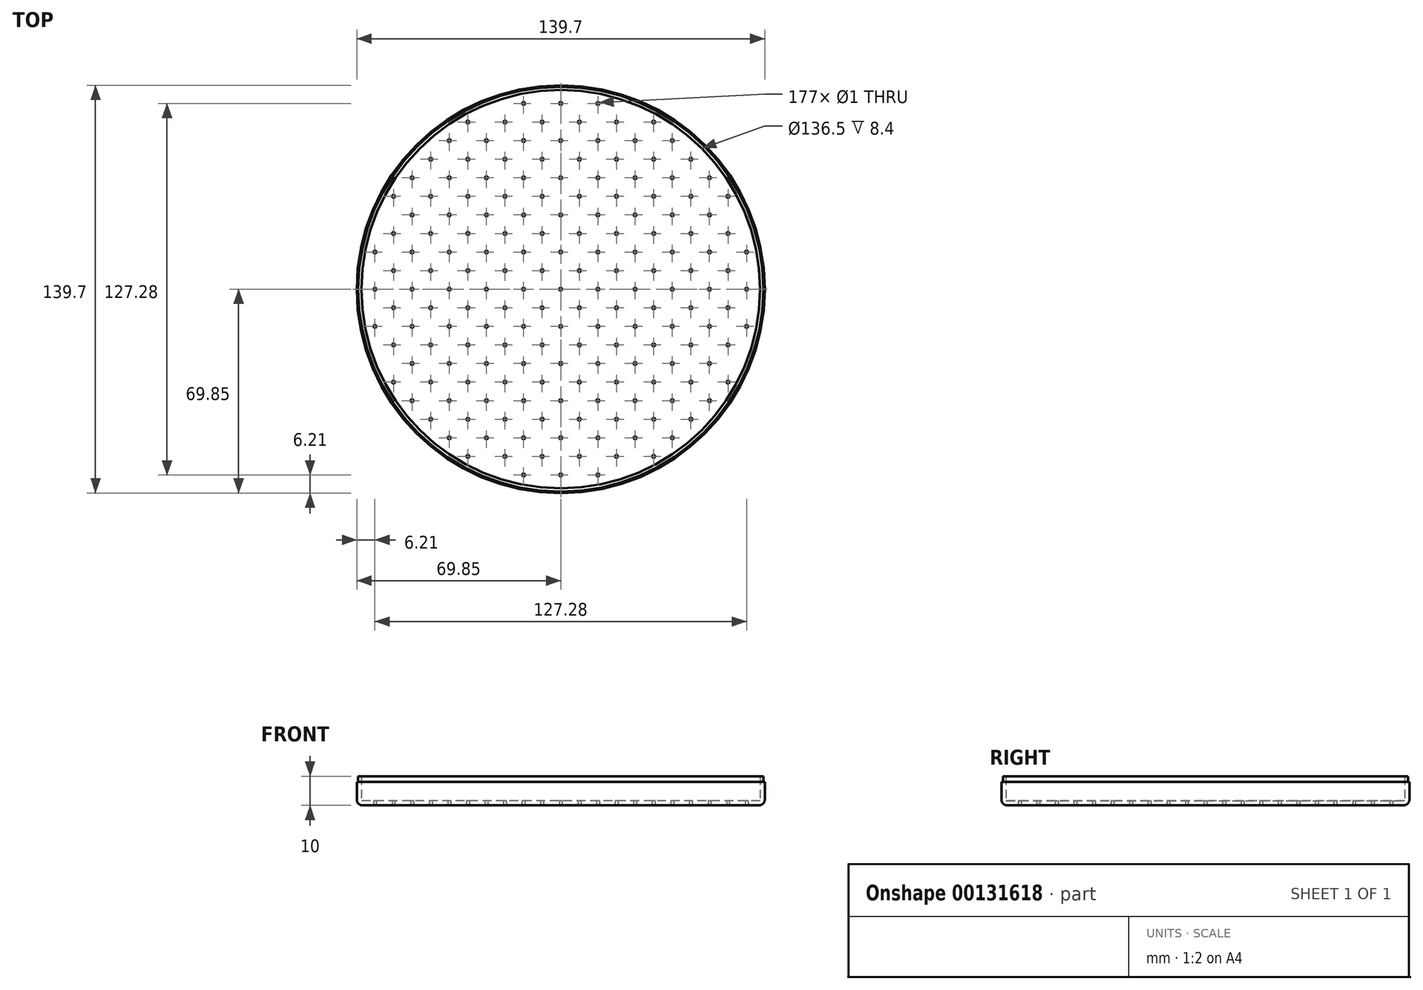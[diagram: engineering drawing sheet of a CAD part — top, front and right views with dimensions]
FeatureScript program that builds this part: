
annotation { "Feature Type Name" : "Feature", "Feature Type Description" : "" }
export const myFeature = defineFeature(function(context is Context, id is Id, definition is map)
    precondition{}
    {
        {
            var Q0;
            Q0=qCreatedBy(makeId("Top.planeOp"),FACE);
            var sketch = newSketch(context, id + "F0", { "sketchPlane" : qUnion([Q0])});
            skCircle(sketch, "E0", {"center": v(0, 0) * mm, "radius": 69.85 * mm});
            skSolve(sketch);
        }
        {
            var Q0;
            Q0=qSketchRegion(id+"F0",true);
            extrude(context, id + "F1", {"entities" : qUnion([Q0]), "depth" : 10 * mm});
        }
        {
            var Q0;
            Q0=makeQuery(id+"F1.opExtrude","CAP_FACE",FACE,{"disambiguationData":[OSD([sQuery(id+"F0.wireOp",EDGE,"E0")])],"isStart":false});
            shell(context, id + "F2", {"entities" : qUnion([Q0]), "thickness" : 1.6 * mm});
        }
        {
            var Q0;
            Q0=makeQuery(id+"F1.opExtrude","CAP_FACE",FACE,{"disambiguationData":[OSD([sQuery(id+"F0.wireOp",EDGE,"E0")])],"isStart":true});
            var sketch = newSketch(context, id + "F3", { "sketchPlane" : qUnion([Q0])});
            skCircle(sketch, "E1", {"center": v(-6.36, 6.36) * mm, "radius": 0.5 * mm});
            skCircle(sketch, "E2.1.0.0", {"center": v(-19.1, 6.36) * mm, "radius": 0.5 * mm});
            skCircle(sketch, "E2.2.0.0", {"center": v(-31.82, 6.36) * mm, "radius": 0.5 * mm});
            skCircle(sketch, "E2.3.0.0", {"center": v(-44.55, 6.36) * mm, "radius": 0.5 * mm});
            skCircle(sketch, "E2.4.0.0", {"center": v(-57.28, 6.36) * mm, "radius": 0.5 * mm});
            skLineSegment(sketch, "E2.direction1", {"start": v(-6.36, 6.36) * mm, "end": v(-19.1, 6.36) * mm, "construction": true});
            skCircle(sketch, "E3", {"center": v(0, 0) * mm, "radius": 0.5 * mm});
            skCircle(sketch, "E4.1.0.0", {"center": v(-12.73, 0) * mm, "radius": 0.5 * mm});
            skCircle(sketch, "E4.2.0.0", {"center": v(-25.46, 0) * mm, "radius": 0.5 * mm});
            skCircle(sketch, "E4.3.0.0", {"center": v(-38.18, 0) * mm, "radius": 0.5 * mm});
            skCircle(sketch, "E4.4.0.0", {"center": v(-50.91, 0) * mm, "radius": 0.5 * mm});
            skCircle(sketch, "E4.5.0.0", {"center": v(-63.64, 0) * mm, "radius": 0.5 * mm});
            skLineSegment(sketch, "E4.direction1", {"start": v(0, 0) * mm, "end": v(-12.73, 0) * mm, "construction": true});
            skLineSegment(sketch, "E5.0.1.0", {"start": v(0, 12.73) * mm, "end": v(-12.73, 12.73) * mm, "construction": true});
            skLineSegment(sketch, "E5.0.1.1", {"start": v(-6.36, 19.1) * mm, "end": v(-19.1, 19.1) * mm, "construction": true});
            skCircle(sketch, "E5.0.1.2", {"center": v(-50.91, 12.73) * mm, "radius": 0.5 * mm});
            skCircle(sketch, "E5.0.1.3", {"center": v(-31.82, 19.1) * mm, "radius": 0.5 * mm});
            skCircle(sketch, "E5.0.1.4", {"center": v(-44.55, 19.1) * mm, "radius": 0.5 * mm});
            skCircle(sketch, "E5.0.1.5", {"center": v(-38.18, 12.73) * mm, "radius": 0.5 * mm});
            skCircle(sketch, "E5.0.1.6", {"center": v(-57.28, 19.1) * mm, "radius": 0.5 * mm});
            skCircle(sketch, "E5.0.1.7", {"center": v(-25.46, 12.73) * mm, "radius": 0.5 * mm});
            skCircle(sketch, "E5.0.1.8", {"center": v(-63.64, 12.73) * mm, "radius": 0.5 * mm});
            skCircle(sketch, "E5.0.1.9", {"center": v(-19.1, 19.1) * mm, "radius": 0.5 * mm});
            skCircle(sketch, "E5.0.1.10", {"center": v(-6.36, 19.1) * mm, "radius": 0.5 * mm});
            skCircle(sketch, "E5.0.1.11", {"center": v(0, 12.73) * mm, "radius": 0.5 * mm});
            skCircle(sketch, "E5.0.1.12", {"center": v(-12.73, 12.73) * mm, "radius": 0.5 * mm});
            skLineSegment(sketch, "E5.0.2.0", {"start": v(0, 25.46) * mm, "end": v(-12.73, 25.46) * mm, "construction": true});
            skLineSegment(sketch, "E5.0.2.1", {"start": v(-6.36, 31.82) * mm, "end": v(-19.1, 31.82) * mm, "construction": true});
            skCircle(sketch, "E5.0.2.2", {"center": v(-50.91, 25.46) * mm, "radius": 0.5 * mm});
            skCircle(sketch, "E5.0.2.3", {"center": v(-31.82, 31.82) * mm, "radius": 0.5 * mm});
            skCircle(sketch, "E5.0.2.4", {"center": v(-44.55, 31.82) * mm, "radius": 0.5 * mm});
            skCircle(sketch, "E5.0.2.5", {"center": v(-38.18, 25.46) * mm, "radius": 0.5 * mm});
            skCircle(sketch, "E5.0.2.6", {"center": v(-57.28, 31.82) * mm, "radius": 0.5 * mm});
            skCircle(sketch, "E5.0.2.7", {"center": v(-25.46, 25.46) * mm, "radius": 0.5 * mm});
            skCircle(sketch, "E5.0.2.9", {"center": v(-19.1, 31.82) * mm, "radius": 0.5 * mm});
            skCircle(sketch, "E5.0.2.10", {"center": v(-6.36, 31.82) * mm, "radius": 0.5 * mm});
            skCircle(sketch, "E5.0.2.11", {"center": v(0, 25.46) * mm, "radius": 0.5 * mm});
            skCircle(sketch, "E5.0.2.12", {"center": v(-12.73, 25.46) * mm, "radius": 0.5 * mm});
            skLineSegment(sketch, "E5.0.3.0", {"start": v(0, 38.18) * mm, "end": v(-12.73, 38.18) * mm, "construction": true});
            skLineSegment(sketch, "E5.0.3.1", {"start": v(-6.36, 44.55) * mm, "end": v(-19.1, 44.55) * mm, "construction": true});
            skCircle(sketch, "E5.0.3.2", {"center": v(-50.91, 38.18) * mm, "radius": 0.5 * mm});
            skCircle(sketch, "E5.0.3.3", {"center": v(-31.82, 44.55) * mm, "radius": 0.5 * mm});
            skCircle(sketch, "E5.0.3.4", {"center": v(-44.55, 44.55) * mm, "radius": 0.5 * mm});
            skCircle(sketch, "E5.0.3.5", {"center": v(-38.18, 38.18) * mm, "radius": 0.5 * mm});
            skCircle(sketch, "E5.0.3.7", {"center": v(-25.46, 38.18) * mm, "radius": 0.5 * mm});
            skCircle(sketch, "E5.0.3.9", {"center": v(-19.1, 44.55) * mm, "radius": 0.5 * mm});
            skCircle(sketch, "E5.0.3.10", {"center": v(-6.36, 44.55) * mm, "radius": 0.5 * mm});
            skCircle(sketch, "E5.0.3.11", {"center": v(0, 38.18) * mm, "radius": 0.5 * mm});
            skCircle(sketch, "E5.0.3.12", {"center": v(-12.73, 38.18) * mm, "radius": 0.5 * mm});
            skLineSegment(sketch, "E5.0.4.0", {"start": v(0, 50.91) * mm, "end": v(-12.73, 50.91) * mm, "construction": true});
            skLineSegment(sketch, "E5.0.4.1", {"start": v(-6.36, 57.28) * mm, "end": v(-19.1, 57.28) * mm, "construction": true});
            skCircle(sketch, "E5.0.4.3", {"center": v(-31.82, 57.28) * mm, "radius": 0.5 * mm});
            skCircle(sketch, "E5.0.4.5", {"center": v(-38.18, 50.91) * mm, "radius": 0.5 * mm});
            skCircle(sketch, "E5.0.4.7", {"center": v(-25.46, 50.91) * mm, "radius": 0.5 * mm});
            skCircle(sketch, "E5.0.4.9", {"center": v(-19.1, 57.28) * mm, "radius": 0.5 * mm});
            skCircle(sketch, "E5.0.4.10", {"center": v(-6.36, 57.28) * mm, "radius": 0.5 * mm});
            skCircle(sketch, "E5.0.4.11", {"center": v(0, 50.91) * mm, "radius": 0.5 * mm});
            skCircle(sketch, "E5.0.4.12", {"center": v(-12.73, 50.91) * mm, "radius": 0.5 * mm});
            skLineSegment(sketch, "E5.0.5.0", {"start": v(0, 63.64) * mm, "end": v(-12.73, 63.64) * mm, "construction": true});
            skCircle(sketch, "E5.0.5.11", {"center": v(0, 63.64) * mm, "radius": 0.5 * mm});
            skCircle(sketch, "E5.0.5.12", {"center": v(-12.73, 63.64) * mm, "radius": 0.5 * mm});
            skLineSegment(sketch, "E5.direction1", {"start": v(-63.64, 0) * mm, "end": v(-38.64, 0) * mm, "construction": true});
            skLineSegment(sketch, "E5.direction2", {"start": v(-63.64, 0) * mm, "end": v(-63.64, 12.73) * mm, "construction": true});
            skCircle(sketch, "E6.MirrorC", {"center": v(63.64, 0) * mm, "radius": 0.5 * mm});
            skCircle(sketch, "E7.MirrorC", {"center": v(6.36, 31.82) * mm, "radius": 0.5 * mm});
            skCircle(sketch, "E8.MirrorC", {"center": v(12.73, 0) * mm, "radius": 0.5 * mm});
            skCircle(sketch, "E9.MirrorC", {"center": v(19.1, 6.36) * mm, "radius": 0.5 * mm});
            skCircle(sketch, "E10.MirrorC", {"center": v(6.36, 6.36) * mm, "radius": 0.5 * mm});
            skCircle(sketch, "E11.MirrorC", {"center": v(19.1, 31.82) * mm, "radius": 0.5 * mm});
            skCircle(sketch, "E12.MirrorC", {"center": v(19.1, 19.1) * mm, "radius": 0.5 * mm});
            skCircle(sketch, "E13.MirrorC", {"center": v(12.73, 50.91) * mm, "radius": 0.5 * mm});
            skCircle(sketch, "E14.MirrorC", {"center": v(12.73, 12.73) * mm, "radius": 0.5 * mm});
            skCircle(sketch, "E15.MirrorC", {"center": v(12.73, 38.18) * mm, "radius": 0.5 * mm});
            skCircle(sketch, "E16.MirrorC", {"center": v(19.1, 57.28) * mm, "radius": 0.5 * mm});
            skCircle(sketch, "E17.MirrorC", {"center": v(12.73, 25.46) * mm, "radius": 0.5 * mm});
            skCircle(sketch, "E18.MirrorC", {"center": v(6.36, 44.55) * mm, "radius": 0.5 * mm});
            skCircle(sketch, "E19.MirrorC", {"center": v(12.73, 63.64) * mm, "radius": 0.5 * mm});
            skCircle(sketch, "E20.MirrorC", {"center": v(63.64, 12.73) * mm, "radius": 0.5 * mm});
            skCircle(sketch, "E21.MirrorC", {"center": v(6.36, 19.1) * mm, "radius": 0.5 * mm});
            skCircle(sketch, "E22.MirrorC", {"center": v(19.1, 44.55) * mm, "radius": 0.5 * mm});
            skCircle(sketch, "E23.MirrorC", {"center": v(6.36, 57.28) * mm, "radius": 0.5 * mm});
            skCircle(sketch, "E24.MirrorC", {"center": v(31.82, 57.28) * mm, "radius": 0.5 * mm});
            skCircle(sketch, "E25.MirrorC", {"center": v(57.28, 19.1) * mm, "radius": 0.5 * mm});
            skCircle(sketch, "E26.MirrorC", {"center": v(44.55, 44.55) * mm, "radius": 0.5 * mm});
            skLineSegment(sketch, "E27.MirrorCS", {"start": v(0, 0) * mm, "end": v(12.73, 0) * mm, "construction": true});
            skCircle(sketch, "E28.MirrorC", {"center": v(50.91, 0) * mm, "radius": 0.5 * mm});
            skCircle(sketch, "E29.MirrorC", {"center": v(38.18, 0) * mm, "radius": 0.5 * mm});
            skCircle(sketch, "E30.MirrorC", {"center": v(25.46, 0) * mm, "radius": 0.5 * mm});
            skCircle(sketch, "E31.MirrorC", {"center": v(57.28, 6.36) * mm, "radius": 0.5 * mm});
            skCircle(sketch, "E32.MirrorC", {"center": v(44.55, 6.36) * mm, "radius": 0.5 * mm});
            skCircle(sketch, "E33.MirrorC", {"center": v(31.82, 6.36) * mm, "radius": 0.5 * mm});
            skCircle(sketch, "E34.MirrorC", {"center": v(50.91, 12.73) * mm, "radius": 0.5 * mm});
            skCircle(sketch, "E35.MirrorC", {"center": v(38.18, 12.73) * mm, "radius": 0.5 * mm});
            skCircle(sketch, "E36.MirrorC", {"center": v(31.82, 44.55) * mm, "radius": 0.5 * mm});
            skCircle(sketch, "E37.MirrorC", {"center": v(25.46, 25.46) * mm, "radius": 0.5 * mm});
            skCircle(sketch, "E38.MirrorC", {"center": v(44.55, 19.1) * mm, "radius": 0.5 * mm});
            skCircle(sketch, "E39.MirrorC", {"center": v(50.91, 38.18) * mm, "radius": 0.5 * mm});
            skCircle(sketch, "E40.MirrorC", {"center": v(25.46, 38.18) * mm, "radius": 0.5 * mm});
            skCircle(sketch, "E41.MirrorC", {"center": v(31.82, 19.1) * mm, "radius": 0.5 * mm});
            skCircle(sketch, "E42.MirrorC", {"center": v(38.18, 25.46) * mm, "radius": 0.5 * mm});
            skCircle(sketch, "E43.MirrorC", {"center": v(38.18, 50.91) * mm, "radius": 0.5 * mm});
            skCircle(sketch, "E44.MirrorC", {"center": v(38.18, 38.18) * mm, "radius": 0.5 * mm});
            skCircle(sketch, "E45.MirrorC", {"center": v(31.82, 31.82) * mm, "radius": 0.5 * mm});
            skCircle(sketch, "E46.MirrorC", {"center": v(50.91, 25.46) * mm, "radius": 0.5 * mm});
            skCircle(sketch, "E47.MirrorC", {"center": v(25.46, 12.73) * mm, "radius": 0.5 * mm});
            skCircle(sketch, "E48.MirrorC", {"center": v(25.46, 50.91) * mm, "radius": 0.5 * mm});
            skCircle(sketch, "E49.MirrorC", {"center": v(44.55, 31.82) * mm, "radius": 0.5 * mm});
            skCircle(sketch, "E50.MirrorC", {"center": v(57.28, 31.82) * mm, "radius": 0.5 * mm});
            skLineSegment(sketch, "E51.MirrorCS", {"start": v(0, 25.46) * mm, "end": v(12.73, 25.46) * mm, "construction": true});
            skLineSegment(sketch, "E52.MirrorCS", {"start": v(0, 63.64) * mm, "end": v(12.73, 63.64) * mm, "construction": true});
            skLineSegment(sketch, "E53.MirrorCS", {"start": v(6.36, 6.36) * mm, "end": v(19.1, 6.36) * mm, "construction": true});
            skLineSegment(sketch, "E54.MirrorCS", {"start": v(6.36, 57.28) * mm, "end": v(19.1, 57.28) * mm, "construction": true});
            skLineSegment(sketch, "E55.MirrorCS", {"start": v(6.36, 19.1) * mm, "end": v(19.1, 19.1) * mm, "construction": true});
            skLineSegment(sketch, "E56.MirrorCS", {"start": v(0, 50.91) * mm, "end": v(12.73, 50.91) * mm, "construction": true});
            skLineSegment(sketch, "E57.MirrorCS", {"start": v(0, 12.73) * mm, "end": v(12.73, 12.73) * mm, "construction": true});
            skLineSegment(sketch, "E58.MirrorCS", {"start": v(0, 38.18) * mm, "end": v(12.73, 38.18) * mm, "construction": true});
            skLineSegment(sketch, "E59.MirrorCS", {"start": v(63.64, 0) * mm, "end": v(38.64, 0) * mm, "construction": true});
            skLineSegment(sketch, "E60.MirrorCS", {"start": v(6.36, 44.55) * mm, "end": v(19.1, 44.55) * mm, "construction": true});
            skLineSegment(sketch, "E61.MirrorCS", {"start": v(63.64, 0) * mm, "end": v(63.64, 12.73) * mm, "construction": true});
            skLineSegment(sketch, "E62.MirrorCS", {"start": v(6.36, 31.82) * mm, "end": v(19.1, 31.82) * mm, "construction": true});
            skCircle(sketch, "E63.MirrorC", {"center": v(0, -63.64) * mm, "radius": 0.5 * mm});
            skCircle(sketch, "E64.MirrorC", {"center": v(0, -25.46) * mm, "radius": 0.5 * mm});
            skCircle(sketch, "E65.MirrorC", {"center": v(0, -38.18) * mm, "radius": 0.5 * mm});
            skCircle(sketch, "E66.MirrorC", {"center": v(0, -50.91) * mm, "radius": 0.5 * mm});
            skCircle(sketch, "E67.MirrorC", {"center": v(0, -12.73) * mm, "radius": 0.5 * mm});
            skCircle(sketch, "E68.MirrorC", {"center": v(-6.36, -31.82) * mm, "radius": 0.5 * mm});
            skCircle(sketch, "E69.MirrorC", {"center": v(6.36, -19.1) * mm, "radius": 0.5 * mm});
            skCircle(sketch, "E70.MirrorC", {"center": v(6.36, -6.36) * mm, "radius": 0.5 * mm});
            skCircle(sketch, "E71.MirrorC", {"center": v(12.73, -38.18) * mm, "radius": 0.5 * mm});
            skCircle(sketch, "E72.MirrorC", {"center": v(19.1, -6.36) * mm, "radius": 0.5 * mm});
            skCircle(sketch, "E73.MirrorC", {"center": v(-12.73, -50.91) * mm, "radius": 0.5 * mm});
            skCircle(sketch, "E74.MirrorC", {"center": v(-12.73, -63.64) * mm, "radius": 0.5 * mm});
            skCircle(sketch, "E75.MirrorC", {"center": v(-63.64, -12.73) * mm, "radius": 0.5 * mm});
            skCircle(sketch, "E76.MirrorC", {"center": v(-6.36, -44.55) * mm, "radius": 0.5 * mm});
            skCircle(sketch, "E77.MirrorC", {"center": v(-12.73, -25.46) * mm, "radius": 0.5 * mm});
            skCircle(sketch, "E78.MirrorC", {"center": v(12.73, -25.46) * mm, "radius": 0.5 * mm});
            skCircle(sketch, "E79.MirrorC", {"center": v(-19.1, -19.1) * mm, "radius": 0.5 * mm});
            skCircle(sketch, "E80.MirrorC", {"center": v(6.36, -57.28) * mm, "radius": 0.5 * mm});
            skCircle(sketch, "E81.MirrorC", {"center": v(-19.1, -57.28) * mm, "radius": 0.5 * mm});
            skCircle(sketch, "E82.MirrorC", {"center": v(19.1, -19.1) * mm, "radius": 0.5 * mm});
            skCircle(sketch, "E83.MirrorC", {"center": v(-12.73, -12.73) * mm, "radius": 0.5 * mm});
            skCircle(sketch, "E84.MirrorC", {"center": v(6.36, -44.55) * mm, "radius": 0.5 * mm});
            skCircle(sketch, "E85.MirrorC", {"center": v(12.73, -12.73) * mm, "radius": 0.5 * mm});
            skCircle(sketch, "E86.MirrorC", {"center": v(-12.73, -38.18) * mm, "radius": 0.5 * mm});
            skCircle(sketch, "E87.MirrorC", {"center": v(-6.36, -19.1) * mm, "radius": 0.5 * mm});
            skCircle(sketch, "E88.MirrorC", {"center": v(-6.36, -57.28) * mm, "radius": 0.5 * mm});
            skCircle(sketch, "E89.MirrorC", {"center": v(12.73, -50.91) * mm, "radius": 0.5 * mm});
            skCircle(sketch, "E90.MirrorC", {"center": v(19.1, -44.55) * mm, "radius": 0.5 * mm});
            skCircle(sketch, "E91.MirrorC", {"center": v(19.1, -31.82) * mm, "radius": 0.5 * mm});
            skCircle(sketch, "E92.MirrorC", {"center": v(6.36, -31.82) * mm, "radius": 0.5 * mm});
            skCircle(sketch, "E93.MirrorC", {"center": v(63.64, -12.73) * mm, "radius": 0.5 * mm});
            skCircle(sketch, "E94.MirrorC", {"center": v(19.1, -57.28) * mm, "radius": 0.5 * mm});
            skCircle(sketch, "E95.MirrorC", {"center": v(-19.1, -6.36) * mm, "radius": 0.5 * mm});
            skCircle(sketch, "E96.MirrorC", {"center": v(-19.1, -31.82) * mm, "radius": 0.5 * mm});
            skCircle(sketch, "E97.MirrorC", {"center": v(-19.1, -44.55) * mm, "radius": 0.5 * mm});
            skCircle(sketch, "E98.MirrorC", {"center": v(12.73, -63.64) * mm, "radius": 0.5 * mm});
            skCircle(sketch, "E99.MirrorC", {"center": v(-6.36, -6.36) * mm, "radius": 0.5 * mm});
            skCircle(sketch, "E100.MirrorC", {"center": v(31.82, -44.55) * mm, "radius": 0.5 * mm});
            skCircle(sketch, "E101.MirrorC", {"center": v(-31.82, -57.28) * mm, "radius": 0.5 * mm});
            skCircle(sketch, "E102.MirrorC", {"center": v(25.46, -25.46) * mm, "radius": 0.5 * mm});
            skCircle(sketch, "E103.MirrorC", {"center": v(50.91, -25.46) * mm, "radius": 0.5 * mm});
            skCircle(sketch, "E104.MirrorC", {"center": v(-31.82, -31.82) * mm, "radius": 0.5 * mm});
            skCircle(sketch, "E105.MirrorC", {"center": v(-25.46, -12.73) * mm, "radius": 0.5 * mm});
            skCircle(sketch, "E106.MirrorC", {"center": v(38.18, -38.18) * mm, "radius": 0.5 * mm});
            skCircle(sketch, "E107.MirrorC", {"center": v(-38.18, -38.18) * mm, "radius": 0.5 * mm});
            skCircle(sketch, "E108.MirrorC", {"center": v(-57.28, -19.1) * mm, "radius": 0.5 * mm});
            skCircle(sketch, "E109.MirrorC", {"center": v(38.18, -50.91) * mm, "radius": 0.5 * mm});
            skCircle(sketch, "E110.MirrorC", {"center": v(-44.55, -44.55) * mm, "radius": 0.5 * mm});
            skCircle(sketch, "E111.MirrorC", {"center": v(-50.91, -12.73) * mm, "radius": 0.5 * mm});
            skCircle(sketch, "E112.MirrorC", {"center": v(-50.91, -25.46) * mm, "radius": 0.5 * mm});
            skCircle(sketch, "E113.MirrorC", {"center": v(-25.46, -38.18) * mm, "radius": 0.5 * mm});
            skCircle(sketch, "E114.MirrorC", {"center": v(31.82, -31.82) * mm, "radius": 0.5 * mm});
            skCircle(sketch, "E115.MirrorC", {"center": v(50.91, -12.73) * mm, "radius": 0.5 * mm});
            skCircle(sketch, "E116.MirrorC", {"center": v(-25.46, -50.91) * mm, "radius": 0.5 * mm});
            skCircle(sketch, "E117.MirrorC", {"center": v(-44.55, -31.82) * mm, "radius": 0.5 * mm});
            skCircle(sketch, "E118.MirrorC", {"center": v(25.46, -12.73) * mm, "radius": 0.5 * mm});
            skCircle(sketch, "E119.MirrorC", {"center": v(44.55, -19.1) * mm, "radius": 0.5 * mm});
            skCircle(sketch, "E120.MirrorC", {"center": v(-50.91, -38.18) * mm, "radius": 0.5 * mm});
            skCircle(sketch, "E121.MirrorC", {"center": v(57.28, -6.36) * mm, "radius": 0.5 * mm});
            skCircle(sketch, "E122.MirrorC", {"center": v(-31.82, -44.55) * mm, "radius": 0.5 * mm});
            skCircle(sketch, "E123.MirrorC", {"center": v(-38.18, -25.46) * mm, "radius": 0.5 * mm});
            skCircle(sketch, "E124.MirrorC", {"center": v(25.46, -50.91) * mm, "radius": 0.5 * mm});
            skCircle(sketch, "E125.MirrorC", {"center": v(44.55, -6.36) * mm, "radius": 0.5 * mm});
            skCircle(sketch, "E126.MirrorC", {"center": v(50.91, -38.18) * mm, "radius": 0.5 * mm});
            skCircle(sketch, "E127.MirrorC", {"center": v(38.18, -25.46) * mm, "radius": 0.5 * mm});
            skCircle(sketch, "E128.MirrorC", {"center": v(44.55, -31.82) * mm, "radius": 0.5 * mm});
            skCircle(sketch, "E129.MirrorC", {"center": v(-57.28, -31.82) * mm, "radius": 0.5 * mm});
            skCircle(sketch, "E130.MirrorC", {"center": v(44.55, -44.55) * mm, "radius": 0.5 * mm});
            skCircle(sketch, "E131.MirrorC", {"center": v(-31.82, -19.1) * mm, "radius": 0.5 * mm});
            skCircle(sketch, "E132.MirrorC", {"center": v(57.28, -31.82) * mm, "radius": 0.5 * mm});
            skCircle(sketch, "E133.MirrorC", {"center": v(57.28, -19.1) * mm, "radius": 0.5 * mm});
            skCircle(sketch, "E134.MirrorC", {"center": v(31.82, -6.36) * mm, "radius": 0.5 * mm});
            skCircle(sketch, "E135.MirrorC", {"center": v(31.82, -19.1) * mm, "radius": 0.5 * mm});
            skCircle(sketch, "E136.MirrorC", {"center": v(-44.55, -19.1) * mm, "radius": 0.5 * mm});
            skCircle(sketch, "E137.MirrorC", {"center": v(-57.28, -6.36) * mm, "radius": 0.5 * mm});
            skCircle(sketch, "E138.MirrorC", {"center": v(-44.55, -6.36) * mm, "radius": 0.5 * mm});
            skCircle(sketch, "E139.MirrorC", {"center": v(-31.82, -6.36) * mm, "radius": 0.5 * mm});
            skCircle(sketch, "E140.MirrorC", {"center": v(-38.18, -50.91) * mm, "radius": 0.5 * mm});
            skCircle(sketch, "E141.MirrorC", {"center": v(-25.46, -25.46) * mm, "radius": 0.5 * mm});
            skCircle(sketch, "E142.MirrorC", {"center": v(38.18, -12.73) * mm, "radius": 0.5 * mm});
            skCircle(sketch, "E143.MirrorC", {"center": v(-38.18, -12.73) * mm, "radius": 0.5 * mm});
            skCircle(sketch, "E144.MirrorC", {"center": v(25.46, -38.18) * mm, "radius": 0.5 * mm});
            skCircle(sketch, "E145.MirrorC", {"center": v(31.82, -57.28) * mm, "radius": 0.5 * mm});
            skLineSegment(sketch, "E146.MirrorCS", {"start": v(0, -63.64) * mm, "end": v(12.73, -63.64) * mm, "construction": true});
            skLineSegment(sketch, "E147.MirrorCS", {"start": v(6.36, -6.36) * mm, "end": v(19.1, -6.36) * mm, "construction": true});
            skLineSegment(sketch, "E148.MirrorCS", {"start": v(6.36, -44.55) * mm, "end": v(19.1, -44.55) * mm, "construction": true});
            skLineSegment(sketch, "E149.MirrorCS", {"start": v(-6.36, -31.82) * mm, "end": v(-19.1, -31.82) * mm, "construction": true});
            skLineSegment(sketch, "E150.MirrorCS", {"start": v(0, -25.46) * mm, "end": v(-12.73, -25.46) * mm, "construction": true});
            skLineSegment(sketch, "E151.MirrorCS", {"start": v(0, -63.64) * mm, "end": v(-12.73, -63.64) * mm, "construction": true});
            skLineSegment(sketch, "E152.MirrorCS", {"start": v(-6.36, -6.36) * mm, "end": v(-19.1, -6.36) * mm, "construction": true});
            skLineSegment(sketch, "E153.MirrorCS", {"start": v(63.64, 0) * mm, "end": v(63.64, -12.73) * mm, "construction": true});
            skLineSegment(sketch, "E154.MirrorCS", {"start": v(-63.64, 0) * mm, "end": v(-63.64, -12.73) * mm, "construction": true});
            skLineSegment(sketch, "E155.MirrorCS", {"start": v(6.36, -57.28) * mm, "end": v(19.1, -57.28) * mm, "construction": true});
            skLineSegment(sketch, "E156.MirrorCS", {"start": v(0, -38.18) * mm, "end": v(-12.73, -38.18) * mm, "construction": true});
            skLineSegment(sketch, "E157.MirrorCS", {"start": v(6.36, -19.1) * mm, "end": v(19.1, -19.1) * mm, "construction": true});
            skLineSegment(sketch, "E158.MirrorCS", {"start": v(-6.36, -19.1) * mm, "end": v(-19.1, -19.1) * mm, "construction": true});
            skLineSegment(sketch, "E159.MirrorCS", {"start": v(-6.36, -44.55) * mm, "end": v(-19.1, -44.55) * mm, "construction": true});
            skLineSegment(sketch, "E160.MirrorCS", {"start": v(0, -38.18) * mm, "end": v(12.73, -38.18) * mm, "construction": true});
            skLineSegment(sketch, "E161.MirrorCS", {"start": v(0, -12.73) * mm, "end": v(12.73, -12.73) * mm, "construction": true});
            skLineSegment(sketch, "E162.MirrorCS", {"start": v(0, -12.73) * mm, "end": v(-12.73, -12.73) * mm, "construction": true});
            skLineSegment(sketch, "E163.MirrorCS", {"start": v(6.36, -31.82) * mm, "end": v(19.1, -31.82) * mm, "construction": true});
            skLineSegment(sketch, "E164.MirrorCS", {"start": v(-6.36, -57.28) * mm, "end": v(-19.1, -57.28) * mm, "construction": true});
            skLineSegment(sketch, "E165.MirrorCS", {"start": v(0, -25.46) * mm, "end": v(12.73, -25.46) * mm, "construction": true});
            skLineSegment(sketch, "E166.MirrorCS", {"start": v(0, -50.91) * mm, "end": v(-12.73, -50.91) * mm, "construction": true});
            skLineSegment(sketch, "E167.MirrorCS", {"start": v(0, -50.91) * mm, "end": v(12.73, -50.91) * mm, "construction": true});
            skSolve(sketch);
        }
        {
            var Q0;
            Q0=qSketchRegion(id+"F3",true);
            extrude(context, id + "F4", {"entities" : qUnion([Q0]), "operationType" : NewBodyOperationType.REMOVE, "endBound" : BoundingType.UP_TO_NEXT, "oppositeDirection" : true, "depth" : 25 * mm});
        }
        {
            var Q0;
            Q0=makeQuery(id+"F1.opExtrude","CAP_EDGE",EDGE,{"disambiguationData":[OSD([sQuery(id+"F0.wireOp",EDGE,"E0")])],"isStart":true});
            fillet(context, id + "F5", {"entities" : qUnion([Q0]), "radius" : 2 * mm, "tangentPropagation" : true, "allowEdgeOverflow" : false});
        }
        {
            var Q0;
            Q0=makeQuery(id+"F1.opExtrude","CAP_FACE",FACE,{"disambiguationData":[OSD([sQuery(id+"F0.wireOp",EDGE,"E0")])],"isStart":false});
            var sketch = newSketch(context, id + "F6", { "sketchPlane" : qUnion([Q0])});
            skCircle(sketch, "E168", {"center": v(0, 0) * mm, "radius": 69.85 * mm});
            skCircle(sketch, "E169", {"center": v(0, 0) * mm, "radius": 69.35 * mm});
            skSolve(sketch);
        }
        {
            var Q0;
            Q0=qSketchRegion(id+"F6",true);
            extrude(context, id + "F7", {"entities" : qUnion([Q0]), "operationType" : NewBodyOperationType.REMOVE, "oppositeDirection" : true, "depth" : 2 * mm});
        }
    });
